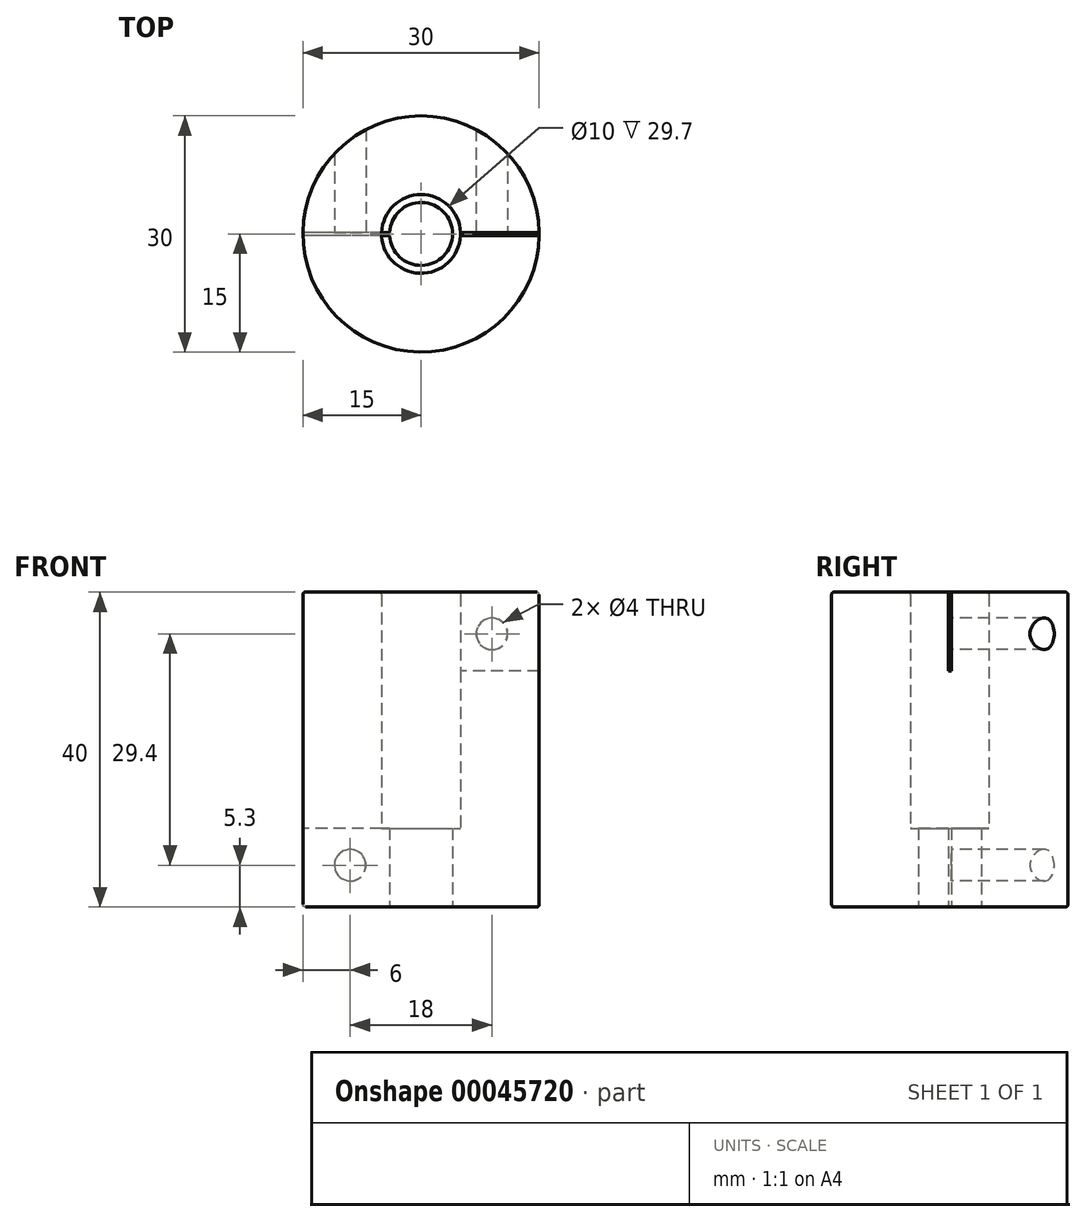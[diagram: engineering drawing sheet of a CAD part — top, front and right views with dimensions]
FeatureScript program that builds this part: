
annotation { "Feature Type Name" : "Feature", "Feature Type Description" : "" }
export const myFeature = defineFeature(function(context is Context, id is Id, definition is map)
    precondition{}
    {
        {
            var Q0;
            Q0=qCreatedBy(makeId("Top.planeOp"),FACE);
            var sketch = newSketch(context, id + "F0", { "sketchPlane" : qUnion([Q0])});
            skCircle(sketch, "E0", {"center": v(0, 0) * mm, "radius": 15 * mm});
            skCircle(sketch, "E1", {"center": v(0, 0) * mm, "radius": 4 * mm});
            skSolve(sketch);
        }
        {
            var Q0;
            Q0=makeQuery(id+"F0.imprint","IMPRINT",FACE,{"disambiguationData":[TD([[makeQuery(id+"F0.imprint","IMPRINT",EDGE,{"derivedFrom":sQuery(id+"F0.wireOp",EDGE,"E0")}),1.0]])]});
            extrude(context, id + "F1", {"entities" : qUnion([Q0]), "depth" : 10 * mm});
        }
        {
            var Q0;
            Q0=makeQuery(id+"F1.opExtrude","CAP_FACE",FACE,{"disambiguationData":[OSD([sQuery(id+"F0.wireOp",EDGE,"E0"),sQuery(id+"F0.wireOp",EDGE,"E1")])],"isStart":false});
            var sketch = newSketch(context, id + "F2", { "sketchPlane" : qUnion([Q0])});
            skCircle(sketch, "E2", {"center": v(0, 0) * mm, "radius": 5 * mm});
            skSolve(sketch);
        }
        {
            var Q0;
            Q0=makeQuery(id+"F2.imprint","IMPRINT",FACE,{"disambiguationData":[TD([[makeQuery(id+"F2.imprint","IMPRINT",EDGE,{"derivedFrom":sQuery(id+"F2.wireOp",EDGE,"E2")}),-1.0]])]});
            extrude(context, id + "F3", {"entities" : qUnion([Q0]), "operationType" : NewBodyOperationType.ADD, "depth" : 30 * mm});
        }
        {
            var Q0;
            Q0=makeQuery(id+"F3.opExtrude","CAP_EDGE",EDGE,{"disambiguationData":[OSD([sQuery(id+"F0.wireOp",EDGE,"E0")])],"isStart":false});
            fillet(context, id + "F4", {"entities" : qUnion([Q0]), "radius" : 0.3 * mm, "tangentPropagation" : true, "allowEdgeOverflow" : false});
        }
        {
            var Q0;
            Q0=makeQuery(id+"F1.opExtrude","CAP_EDGE",EDGE,{"disambiguationData":[OSD([sQuery(id+"F0.wireOp",EDGE,"E0")])],"isStart":true});
            var Q1;
            Q1=makeQuery(id+"F3.opExtrude","CAP_EDGE",EDGE,{"disambiguationData":[OSD([sQuery(id+"F2.wireOp",EDGE,"E2")])],"isStart":false});
            var Q2;
            Q2=makeQuery(id+"F1.opExtrude","CAP_EDGE",EDGE,{"disambiguationData":[OSD([sQuery(id+"F0.wireOp",EDGE,"E1")])],"isStart":true});
            fillet(context, id + "F5", {"entities" : qUnion([Q0, Q1, Q2]), "radius" : 0.3 * mm, "tangentPropagation" : true, "allowEdgeOverflow" : false});
        }
        {
            var Q0;
            Q0=qCreatedBy(makeId("Front.planeOp"),FACE);
            var sketch = newSketch(context, id + "F6", { "sketchPlane" : qUnion([Q0])});
            skCircle(sketch, "E3", {"center": v(9, 34.7) * mm, "radius": 2 * mm});
            skCircle(sketch, "E4", {"center": v(-9, 5.3) * mm, "radius": 2 * mm});
            skSolve(sketch);
        }
        {
            var Q0;
            Q0 = qSketchRegion(id + "F6", true);
            extrude(context, id + "F7", {"entities" : qUnion([Q0]), "operationType" : NewBodyOperationType.REMOVE, "oppositeDirection" : true, "depth" : 20.34 * mm});
        }
        {
            var Q0;
            Q0=makeQuery(id+"F3.opExtrude","CAP_FACE",FACE,{"disambiguationData":[OSD([sQuery(id+"F0.wireOp",EDGE,"E0"),sQuery(id+"F2.wireOp",EDGE,"E2")])],"isStart":false});
            var sketch = newSketch(context, id + "F8", { "sketchPlane" : qUnion([Q0])});
            skLineSegment(sketch, "E5.rect.bottom", {"start": v(17, -0.18) * mm, "end": v(2.58, -0.18) * mm});
            skLineSegment(sketch, "E5.rect.top", {"start": v(17, 0.18) * mm, "end": v(2.58, 0.18) * mm});
            skLineSegment(sketch, "E5.rect.left", {"start": v(17, -0.18) * mm, "end": v(17, 0.18) * mm});
            skLineSegment(sketch, "E5.rect.right", {"start": v(2.58, -0.18) * mm, "end": v(2.58, 0.18) * mm});
            skPoint(sketch, "E5.rect.middle", {"position": v(9.8, 0) * mm});
            skSolve(sketch);
        }
        {
            var Q0;
            {var subQ6=sQuery(id+"F8.wireOp",EDGE,"E5.rect.right");Q0=makeQuery(id+"F8.imprint","IMPRINT",FACE,{"disambiguationData":[TD([[makeQuery(id+"F8.imprint","IMPRINT",EDGE,{"derivedFrom":subQ6}),-1.0]])]});}
            var Q1;
            {var subQ0=sQuery(id+"F2.wireOp",EDGE,"E2");var subQ1=sQuery(id+"F0.wireOp",EDGE,"E0");var subQ2=makeQuery(id+"F3.opExtrude","CAP_FACE",FACE,{"disambiguationData":[OSD([subQ1,subQ0])],"isStart":false});var subQ6=sQuery(id+"F8.wireOp",EDGE,"E5.rect.bottom");var subQ8=makeQuery(id+"F4.opFillet","BLEND_EDGE",EDGE,{"blendedFrom":[makeQuery(id+"F3.opExtrude","CAP_EDGE",EDGE,{"disambiguationData":[OSD([subQ1])],"isStart":false}),subQ2],"blendedInto":[subQ2]});var subQ10=makeQuery(id+"F8.imprint","INTERSECT",VERTEX,{"derivedFrom":[subQ8,subQ6]});Q1=makeQuery(id+"F8.imprint","IMPRINT",FACE,{"disambiguationData":[TD([[makeQuery(id+"F8.imprint","IMPRINT",EDGE,{"disambiguationData":[TD([[subQ10,-1.0]])],"derivedFrom":subQ6}),-1.0]])]});}
            var Q2;
            {var subQ6=sQuery(id+"F8.wireOp",EDGE,"E5.rect.left");Q2=makeQuery(id+"F8.imprint","IMPRINT",FACE,{"disambiguationData":[TD([[makeQuery(id+"F8.imprint","IMPRINT",EDGE,{"derivedFrom":subQ6}),1.0]])]});}
            extrude(context, id + "F9", {"entities" : qUnion([Q0, Q1, Q2]), "operationType" : NewBodyOperationType.REMOVE, "oppositeDirection" : true, "depth" : 10 * mm});
        }
        {
            var Q0;
            Q0=makeQuery(id+"F1.opExtrude","CAP_FACE",FACE,{"disambiguationData":[OSD([sQuery(id+"F0.wireOp",EDGE,"E0"),sQuery(id+"F0.wireOp",EDGE,"E1")])],"isStart":true});
            var sketch = newSketch(context, id + "F10", { "sketchPlane" : qUnion([Q0])});
            skLineSegment(sketch, "E6.rect.bottom", {"start": v(-1.98, -0.18) * mm, "end": v(-16.4, -0.18) * mm});
            skLineSegment(sketch, "E6.rect.top", {"start": v(-1.98, 0.18) * mm, "end": v(-16.4, 0.18) * mm});
            skLineSegment(sketch, "E6.rect.left", {"start": v(-1.98, -0.18) * mm, "end": v(-1.98, 0.18) * mm});
            skLineSegment(sketch, "E6.rect.right", {"start": v(-16.4, -0.18) * mm, "end": v(-16.4, 0.18) * mm});
            skPoint(sketch, "E6.rect.middle", {"position": v(-9.19, 0) * mm});
            skSolve(sketch);
        }
        {
            var Q0;
            {var subQ6=sQuery(id+"F10.wireOp",EDGE,"E6.rect.left");Q0=makeQuery(id+"F10.imprint","IMPRINT",FACE,{"disambiguationData":[TD([[makeQuery(id+"F10.imprint","IMPRINT",EDGE,{"derivedFrom":subQ6}),1.0]])]});}
            var Q1;
            {var subQ0=sQuery(id+"F0.wireOp",EDGE,"E1");var subQ1=sQuery(id+"F0.wireOp",EDGE,"E0");var subQ2=makeQuery(id+"F1.opExtrude","CAP_FACE",FACE,{"disambiguationData":[OSD([subQ1,subQ0])],"isStart":true});var subQ6=sQuery(id+"F10.wireOp",EDGE,"E6.rect.bottom");var subQ8=makeQuery(id+"F5.opFillet","BLEND_EDGE",EDGE,{"blendedFrom":[makeQuery(id+"F1.opExtrude","CAP_EDGE",EDGE,{"disambiguationData":[OSD([subQ1])],"isStart":true}),subQ2],"blendedInto":[subQ2]});var subQ10=makeQuery(id+"F10.imprint","INTERSECT",VERTEX,{"derivedFrom":[subQ8,subQ6]});Q1=makeQuery(id+"F10.imprint","IMPRINT",FACE,{"disambiguationData":[TD([[makeQuery(id+"F10.imprint","IMPRINT",EDGE,{"disambiguationData":[TD([[subQ10,1.0]])],"derivedFrom":subQ6}),-1.0]])]});}
            var Q2;
            {var subQ6=sQuery(id+"F10.wireOp",EDGE,"E6.rect.right");Q2=makeQuery(id+"F10.imprint","IMPRINT",FACE,{"disambiguationData":[TD([[makeQuery(id+"F10.imprint","IMPRINT",EDGE,{"derivedFrom":subQ6}),-1.0]])]});}
            extrude(context, id + "F11", {"entities" : qUnion([Q0, Q1, Q2]), "operationType" : NewBodyOperationType.REMOVE, "oppositeDirection" : true, "depth" : 10 * mm});
        }
    });
